# Revit family: Building-IEC309Connections-GEWISS-IEC309BTS-10°_FLUSH-MOUNT_SOCKET_20-25V_IP44
name_source: partatom
category: Apparecchi elettrici
units: mm (PartAtom-declared; Revit-internal decimal feet)

## family parameters
Condiviso = No
Host = Superficie
Mantenere orientamento annotazione = Sì
Punto di calcolo locali = Sì
Quota connettore circolare = Usa diametro
Taglio con vuoti quando caricato = No
Tipo di parte = Normale

## types (18) — shared parameters
BLOCCO = B=C
Catalogue = BUILDING
Corpo centrale = Default(2)
Electrocod = 2210
FORMULA = 1000 mm  [stored 3.28084 ft]
Flange dimensions (mm) = 85x75
Glow wire test: = 850 °C (active parts) - 650 °C (passive parts)
IDF = 808d92d3-ab0e-4d2e-8f13-4af79e3487d6
IDT = 8afe203aa1864dc1852bbf52b3636d03
IP degree = IP44
Immagine tipo = <Nessuno>
Insulation resistance = - 10 M?
L = 155 mm
Operating temperature: = -25 +40 °C
Piastra = Default(2)
Produttore = GEWISS S.p.A.
Prospetto di default = 500 mm
SEO = Socket outlet
SPinotto = Default(2)
Shock resistance = IK08
Sportello_visibile = Sì
Spostamento_S = 950 mm
Technical sheet = https://www.gewiss.com
Thermo-pressure with ball = 125 °C (active parts) - 80 °C (passive parts)
Type of wiring = With screw
Typology = 10° angled flush-mounting socket-outlet
URL = https://www.gewiss.com
Version file RFA = 21.11
W = 115 mm

## per-type parameters (varying)
| type | Breaking capacity at 1.1 Un | Colour: | Descrizione | Frequency | Modello | No. of poles | Permissible overload | Rated current (A) | Rated voltage: | Reference h: | Terminal tightening capacity | Total number of operations |
| GW62265 - IP44 10°P.RECEPTACLE 2P 16A 24V N.R. | 20A | Violet | IP44 10°P.RECEPTACLE 2P 16A 24V N.R. | 50 - 60 Hz | GW62265 | 2P | 22A | 16 | 20-25 V | - | 1-2.5mm² flexible cables - 1.5-4mm² rigid cables | -5000 |
| GW62267 - IP44 10°P.RECEPTACLE 2P 16A 42V 12H | 20A | White | IP44 10°P.RECEPTACLE 2P 16A 42V 12H | 50 - 60 Hz | GW62267 | 2P | 22A | 16 | 40-50 V | 12 | 1-2.5mm² flexible cables - 1.5-4mm² rigid cables | -5000 |
| GW62281 - IP44 10°P.RECEPTACLE 3P 32A 24/42V 11H | 40A | Green | IP44 10°P.RECEPTACLE 3P 32A 24/42V 11H | 401 - 500 Hz | GW62281 | 3P | 42A | 32 | 20-25V and 40-50 V | 11 | 2.5-6mm² flexible cables - 2.5-10mm² rigid cables | -2000 |
| GW62280 - IP44 10°P.RECEPTACLE 2P 32A 24/42V 11H | 40A | Green | IP44 10°P.RECEPTACLE 2P 32A 24/42V 11H | 401 - 500 Hz | GW62280 | 2P | 42A | 32 | 20-25V and 40-50 V | 11 | 2.5-6mm² flexible cables - 2.5-10mm² rigid cables | -2000 |
| GW62272 - IP44 10°P.RECEPTACLE 3P 16A 42V 11H | 20A | Green | IP44 10°P.RECEPTACLE 3P 16A 42V 11H | 401 - 500 Hz | GW62272 | 3P | 22A | 16 | 20-25V and 40-50 V | 11 | 1-2.5mm² flexible cables - 1.5-4mm² rigid cables | -5000 |
| GW62279 - IP44 10°P.RECEPTACLE 3P 32A 24/42V4H | 40A | Green | IP44 10°P.RECEPTACLE 3P 32A 24/42V4H | 100 - 200 Hz | GW62279 | 3P | 42A | 32 | 20-25V and 40-50 V | 4 | 2.5-6mm² flexible cables - 2.5-10mm² rigid cables | -2000 |
| GW62274 - IP44 10°P.RECEPTACLE 2P 32A 24V N.R. | 40A | Violet | IP44 10°P.RECEPTACLE 2P 32A 24V N.R. | 50 - 60 Hz | GW62274 | 2P | 42A | 32 | 20-25 V | - | 2.5-6mm² flexible cables - 2.5-10mm² rigid cables | -2000 |
| GW62276 - IP44 10°P.RECEPTACLE 2P 32A 24/42V 12H | 40A | White | IP44 10°P.RECEPTACLE 2P 32A 24/42V 12H | 50 - 60 Hz | GW62276 | 2P | 42A | 32 | 40-50 V | 12 | 2.5-6mm² flexible cables - 2.5-10mm² rigid cables | -2000 |
| GW62271 - IP44 10°P.RECEPTACLE 2P 16A 24/42V 11H | 20A | Green | IP44 10°P.RECEPTACLE 2P 16A 24/42V 11H | 401 - 500 Hz | GW62271 | 2P | 22A | 16 | 20-25V and 40-50 V | 11 | 1-2.5mm² flexible cables - 1.5-4mm² rigid cables | -5000 |
| GW62275 - IP44 10°P.RECEPTACLE 3P 32A 24V N.R. | 40A | Violet | IP44 10°P.RECEPTACLE 3P 32A 24V N.R. | 50 - 60 Hz | GW62275 | 3P | 42A | 32 | 20-25 V | - | 2.5-6mm² flexible cables - 2.5-10mm² rigid cables | -2000 |
| GW62277 - IP44 10°P.RECEPTACLE 3P 32A 42V 12H | 40A | White | IP44 10°P.RECEPTACLE 3P 32A 42V 12H | 50 - 60 Hz | GW62277 | 3P | 42A | 32 | 40-50 V | 12 | 2.5-6mm² flexible cables - 2.5-10mm² rigid cables | -2000 |
| GW62266 - IP44 10°P.RECEPTACLE 3P 16A 24V N.R. | 20A | Violet | IP44 10°P.RECEPTACLE 3P 16A 24V N.R. | 50 - 60 Hz | GW62266 | 3P | 22A | 16 | 20-25 V | - | 1-2.5mm² flexible cables - 1.5-4mm² rigid cables | -5000 |
| GW62282 - IP44 10°P.RECEPTACLE 2P 32A CC 10H | 40A | White | IP44 10°P.RECEPTACLE 2P 32A CC 10H | d.c. | GW62282 | 2P | 42A | 32 | 20-25V and 40-50 V | 10 | 2.5-6mm² flexible cables - 2.5-10mm² rigid cables | -2000 |
| GW62278 - IP44 10°P.RECEPTACLE 2P 32A 24/42V4H | 40A | Green | IP44 10°P.RECEPTACLE 2P 32A 24/42V4H | 100 - 200 Hz | GW62278 | 2P | 42A | 32 | 20-25V and 40-50 V | 4 | 2.5-6mm² flexible cables - 2.5-10mm² rigid cables | -2000 |
| GW62273 - IP44 10°P.RECEPTACLE 2P 16A CC 10H | 20A | White | IP44 10°P.RECEPTACLE 2P 16A CC 10H | d.c. | GW62273 | 2P | 22A | 16 | 20-25V and 40-50 V | 10 | 1-2.5mm² flexible cables - 1.5-4mm² rigid cables | -5000 |
| GW62269 - IP44 10°P.RECEPTACLE 2P 16A 24/42V 4H | 20A | Green | IP44 10°P.RECEPTACLE 2P 16A 24/42V 4H | 100 - 200 Hz | GW62269 | 2P | 22A | 16 | 20-25V and 40-50 V | 4 | 1-2.5mm² flexible cables - 1.5-4mm² rigid cables | -5000 |
| GW62270 - IP44 10°P.RECEPTACLE 3P 16A 24/42V 4H | 20A | Green | IP44 10°P.RECEPTACLE 3P 16A 24/42V 4H | 100 - 200 Hz | GW62270 | 3P | 22A | 16 | 20-25V and 40-50 V | 4 | 1-2.5mm² flexible cables - 1.5-4mm² rigid cables | -5000 |
| GW62268 - IP44 10°P.RECEPTACLE 3P 16A 42V 12H | 20A | White | IP44 10°P.RECEPTACLE 3P 16A 42V 12H | 50 - 60 Hz | GW62268 | 3P | 22A | 16 | 40-50 V | 12 | 1-2.5mm² flexible cables - 1.5-4mm² rigid cables | -5000 |

note: [stored X ft] marks values corroborated as IEEE doubles in the binary element streams (Revit-internal decimal feet)

## geometry (parser evidence)
native form markers: Sweep x2
no freeform markers — native parametric forms only
